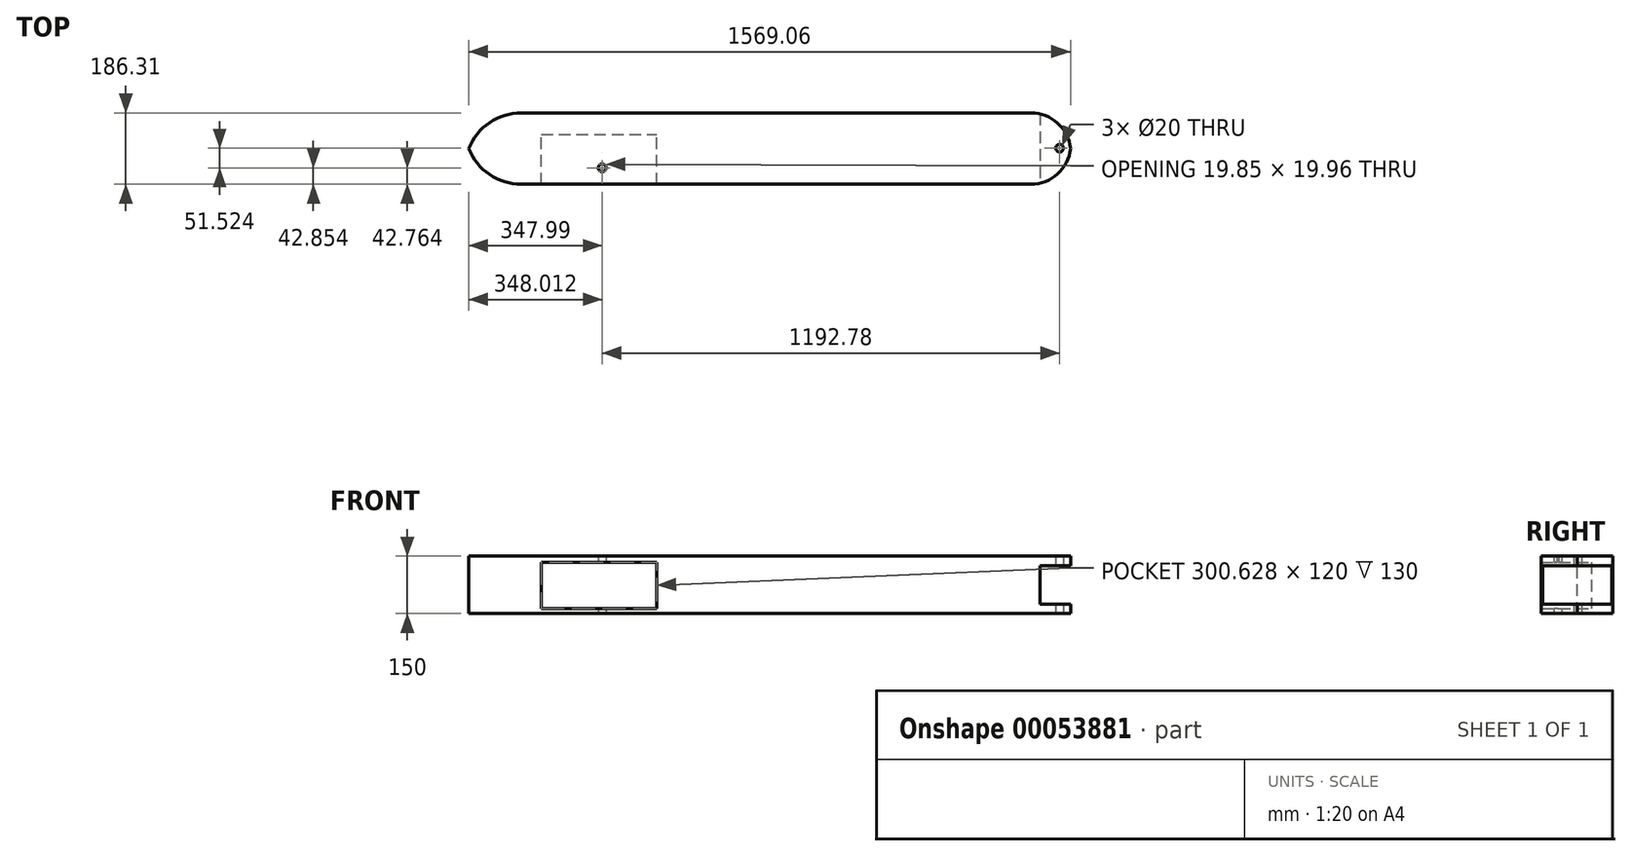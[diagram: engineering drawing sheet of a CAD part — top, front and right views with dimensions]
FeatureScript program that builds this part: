
annotation { "Feature Type Name" : "Feature", "Feature Type Description" : "" }
export const myFeature = defineFeature(function(context is Context, id is Id, definition is map)
    precondition{}
    {
        {
            var Q0;
            Q0=qCreatedBy(makeId("Front.planeOp"),FACE);
            var sketch = newSketch(context, id + "F0", { "sketchPlane" : qUnion([Q0])});
            skLineSegment(sketch, "E0.bottom", {"start": v(-454.56, 147.44) * mm, "end": v(1045.44, 147.44) * mm});
            skLineSegment(sketch, "E0.top", {"start": v(-454.56, -2.56) * mm, "end": v(1045.44, -2.56) * mm});
            skLineSegment(sketch, "E0.left", {"start": v(-454.56, 147.44) * mm, "end": v(-454.56, -2.56) * mm});
            skLineSegment(sketch, "E0.right", {"start": v(1045.44, 147.44) * mm, "end": v(1045.44, -2.56) * mm});
            skSolve(sketch);
        }
        {
            var Q0;
            Q0=makeQuery(id+"F0.imprint","IMPRINT",FACE,{"disambiguationData":[TD([[makeQuery(id+"F0.imprint","IMPRINT",EDGE,{"derivedFrom":sQuery(id+"F0.wireOp",EDGE,"E0.bottom")}),-1.0]])]});
            var Q1;
            Q1=makeQuery(id+"F0.imprint","IMPRINT",FACE,{"disambiguationData":[TD([[makeQuery(id+"F0.imprint","IMPRINT",EDGE,{"derivedFrom":sQuery(id+"F0.wireOp",EDGE,"f0e6ab77-5583-4a0c-8637-5662e6611f36.bottom")}),-1.0]])]});
            extrude(context, id + "F1", {"entities" : qUnion([Q0, Q1]), "depth" : 56.3 * mm});
        }
        {
            var Q0;
            Q0=makeQuery(id+"F1.opExtrude","CAP_FACE",FACE,{"disambiguationData":[OSD([sQuery(id+"F0.wireOp",EDGE,"E0.bottom"),sQuery(id+"F0.wireOp",EDGE,"E0.top"),sQuery(id+"F0.wireOp",EDGE,"E0.left"),sQuery(id+"F0.wireOp",EDGE,"E0.right")])],"isStart":false});
            var sketch = newSketch(context, id + "F2", { "sketchPlane" : qUnion([Q0])});
            skLineSegment(sketch, "E1.bottom", {"start": v(-254.92, 130.96) * mm, "end": v(45.7, 130.96) * mm});
            skLineSegment(sketch, "E1.top", {"start": v(-254.92, 10.96) * mm, "end": v(45.7, 10.96) * mm});
            skLineSegment(sketch, "E1.left", {"start": v(-254.92, 130.96) * mm, "end": v(-254.92, 10.96) * mm});
            skLineSegment(sketch, "E1.right", {"start": v(45.7, 130.96) * mm, "end": v(45.7, 10.96) * mm});
            skSolve(sketch);
        }
        {
            var Q0;
            Q0=makeQuery(id+"F2.imprint","IMPRINT",FACE,{"disambiguationData":[TD([[makeQuery(id+"F2.imprint","IMPRINT",EDGE,{"derivedFrom":sQuery(id+"F2.wireOp",EDGE,"E1.bottom")}),1.0]])]});
            extrude(context, id + "F3", {"entities" : qUnion([Q0]), "operationType" : NewBodyOperationType.ADD, "depth" : 130 * mm});
        }
        {
            var Q0;
            Q0=makeQuery(id+"F3.opExtrude","SWEPT_FACE",FACE,{"disambiguationData":[OSD([sQuery(id+"F2.wireOp",EDGE,"E1.bottom")])]});
            var sketch = newSketch(context, id + "F4", { "sketchPlane" : qUnion([Q0])});
            skCircle(sketch, "E2", {"center": v(-96.12, 143.37) * mm, "radius": 16.52 * mm});
            skCircle(sketch, "E3", {"center": v(-96.12, 143.37) * mm, "radius": 16.28 * mm});
            skSolve(sketch);
        }
        {
            var Q0;
            {var subQ0=sQuery(id+"F0.wireOp",EDGE,"E0.top");Q0=makeQuery(id+"F3.boolean.opBoolean","MERGE",FACE,{"derivedFrom":[makeQuery(id+"F1.opExtrude","SWEPT_FACE",FACE,{"disambiguationData":[OSD([subQ0])]}),makeQuery(id+"F3.opExtrude","SWEPT_FACE",FACE,{"disambiguationData":[OSD([subQ0])]})]});}
            var sketch = newSketch(context, id + "F5", { "sketchPlane" : qUnion([Q0])});
            skCircle(sketch, "E4", {"center": v(-96.16, 143.55) * mm, "radius": 15.74 * mm});
            skSolve(sketch);
        }
        {
            var Q0;
            Q0=sQuery(id+"F4.wireOp",VERTEX,"E3.center");
            var Q1;
            Q1=makeQuery(id+"F1.opExtrude","SWEPT_BODY",BODY,{"disambiguationData":[OSD([sQuery(id+"F0.wireOp",EDGE,"E0.bottom"),sQuery(id+"F0.wireOp",EDGE,"E0.top"),sQuery(id+"F0.wireOp",EDGE,"E0.left"),sQuery(id+"F0.wireOp",EDGE,"E0.right")])]});
            hole(context, id + "F6", {"style" : HoleStyle.SIMPLE, "holeDiameter" : 20 * mm, "endStyle" : HoleEndStyle.THROUGH, "locations" : qUnion([Q0]), "scope" : qUnion([Q1])});
        }
        {
            var Q0;
            Q0=sQuery(id+"F5.wireOp",VERTEX,"E4.center");
            var Q1;
            Q1=makeQuery(id+"F1.opExtrude","SWEPT_BODY",BODY,{"disambiguationData":[OSD([sQuery(id+"F0.wireOp",EDGE,"E0.bottom"),sQuery(id+"F0.wireOp",EDGE,"E0.top"),sQuery(id+"F0.wireOp",EDGE,"E0.left"),sQuery(id+"F0.wireOp",EDGE,"E0.right")])]});
            hole(context, id + "F7", {"style" : HoleStyle.SIMPLE, "holeDiameter" : 20 * mm, "endStyle" : HoleEndStyle.THROUGH, "locations" : qUnion([Q0]), "scope" : qUnion([Q1])});
        }
        {
            var Q0;
            Q0=makeQuery(id+"F3.opExtrude","CAP_EDGE",EDGE,{"disambiguationData":[OSD([sQuery(id+"F0.wireOp",EDGE,"E0.left")])],"isStart":false});
            var Q1;
            Q1=makeQuery(id+"F1.opExtrude","CAP_EDGE",EDGE,{"disambiguationData":[OSD([sQuery(id+"F0.wireOp",EDGE,"E0.left")])],"isStart":true});
            fillet(context, id + "F8", {"entities" : qUnion([Q0, Q1]), "radius" : 147.58 * mm, "tangentPropagation" : true, "allowEdgeOverflow" : false});
        }
        {
            var Q0;
            {var subQ0=sQuery(id+"F0.wireOp",EDGE,"E0.right");Q0=makeQuery(id+"F3.boolean.opBoolean","MERGE",FACE,{"derivedFrom":[makeQuery(id+"F1.opExtrude","SWEPT_FACE",FACE,{"disambiguationData":[OSD([subQ0])]}),makeQuery(id+"F3.opExtrude","SWEPT_FACE",FACE,{"disambiguationData":[OSD([subQ0])]})]});}
            var sketch = newSketch(context, id + "F9", { "sketchPlane" : qUnion([Q0])});
            skLineSegment(sketch, "E5.bottom", {"start": v(0, 122.44) * mm, "end": v(-186.3, 122.44) * mm});
            skLineSegment(sketch, "E5.top", {"start": v(0, 22.44) * mm, "end": v(-186.3, 22.44) * mm});
            skLineSegment(sketch, "E5.left", {"start": v(0, 122.44) * mm, "end": v(0, 22.44) * mm});
            skLineSegment(sketch, "E5.right", {"start": v(-186.3, 122.44) * mm, "end": v(-186.3, 22.44) * mm});
            skSolve(sketch);
        }
        {
            var Q0;
            {var subQ0=sQuery(id+"F9.wireOp",EDGE,"E5.bottom");Q0=makeQuery(id+"F9.imprint","IMPRINT",FACE,{"disambiguationData":[TD([[makeQuery(id+"F9.imprint","IMPRINT",EDGE,{"derivedFrom":subQ0}),-1.0]])]});}
            var Q1;
            {var subQ0=sQuery(id+"F9.wireOp",EDGE,"E5.top");Q1=makeQuery(id+"F9.imprint","IMPRINT",FACE,{"disambiguationData":[TD([[makeQuery(id+"F9.imprint","IMPRINT",EDGE,{"derivedFrom":subQ0}),1.0]])]});}
            extrude(context, id + "F10", {"entities" : qUnion([Q0, Q1]), "operationType" : NewBodyOperationType.ADD, "depth" : 80 * mm});
        }
        {
            var Q0;
            {var subQ0=sQuery(id+"F0.wireOp",EDGE,"E0.right");var subQ2=makeQuery(id+"F1.opExtrude","CAP_EDGE",EDGE,{"disambiguationData":[OSD([subQ0])],"isStart":true});Q0=makeQuery(id+"F10.opExtrude","CAP_EDGE",EDGE,{"disambiguationData":[OSD([subQ0]),TDD([makeQuery(id+"F9.imprint","IMPRINT",EDGE,{"disambiguationData":[TD([[makeQuery(id+"F9.imprint","INTERSECT",VERTEX,{"derivedFrom":[subQ2,sQuery(id+"F9.wireOp",EDGE,"E5.bottom"),sQuery(id+"F9.wireOp",EDGE,"E5.left")]}),1.0]])],"derivedFrom":subQ2})])],"isStart":false});}
            var Q1;
            {var subQ0=sQuery(id+"F0.wireOp",EDGE,"E0.right");var subQ2=makeQuery(id+"F1.opExtrude","CAP_EDGE",EDGE,{"disambiguationData":[OSD([subQ0])],"isStart":true});Q1=makeQuery(id+"F10.opExtrude","CAP_EDGE",EDGE,{"disambiguationData":[OSD([subQ0]),TDD([makeQuery(id+"F9.imprint","IMPRINT",EDGE,{"disambiguationData":[TD([[makeQuery(id+"F9.imprint","INTERSECT",VERTEX,{"derivedFrom":[subQ2,sQuery(id+"F9.wireOp",EDGE,"E5.top"),sQuery(id+"F9.wireOp",EDGE,"E5.left")]}),-1.0]])],"derivedFrom":subQ2})])],"isStart":false});}
            var Q2;
            {var subQ0=sQuery(id+"F0.wireOp",EDGE,"E0.right");var subQ2=makeQuery(id+"F3.opExtrude","CAP_EDGE",EDGE,{"disambiguationData":[OSD([subQ0])],"isStart":false});Q2=makeQuery(id+"F10.opExtrude","CAP_EDGE",EDGE,{"disambiguationData":[OSD([subQ0]),TDD([makeQuery(id+"F9.imprint","IMPRINT",EDGE,{"disambiguationData":[TD([[makeQuery(id+"F9.imprint","INTERSECT",VERTEX,{"derivedFrom":[subQ2,sQuery(id+"F9.wireOp",EDGE,"E5.top"),sQuery(id+"F9.wireOp",EDGE,"E5.right")]}),-1.0]])],"derivedFrom":subQ2})])],"isStart":false});}
            var Q3;
            {var subQ0=sQuery(id+"F0.wireOp",EDGE,"E0.right");var subQ2=makeQuery(id+"F3.opExtrude","CAP_EDGE",EDGE,{"disambiguationData":[OSD([subQ0])],"isStart":false});Q3=makeQuery(id+"F10.opExtrude","CAP_EDGE",EDGE,{"disambiguationData":[OSD([subQ0]),TDD([makeQuery(id+"F9.imprint","IMPRINT",EDGE,{"disambiguationData":[TD([[makeQuery(id+"F9.imprint","INTERSECT",VERTEX,{"derivedFrom":[subQ2,sQuery(id+"F9.wireOp",EDGE,"E5.bottom"),sQuery(id+"F9.wireOp",EDGE,"E5.right")]}),1.0]])],"derivedFrom":subQ2})])],"isStart":false});}
            fillet(context, id + "F11", {"entities" : qUnion([Q0, Q1, Q2, Q3]), "radius" : 103.66 * mm, "tangentPropagation" : true, "allowEdgeOverflow" : false});
        }
        {
            var Q0;
            {var subQ0=sQuery(id+"F0.wireOp",EDGE,"E0.top");Q0=makeQuery(id+"F10.boolean.opBoolean","MERGE",FACE,{"derivedFrom":[makeQuery(id+"F3.boolean.opBoolean","MERGE",FACE,{"derivedFrom":[makeQuery(id+"F1.opExtrude","SWEPT_FACE",FACE,{"disambiguationData":[OSD([subQ0])]}),makeQuery(id+"F3.opExtrude","SWEPT_FACE",FACE,{"disambiguationData":[OSD([subQ0])]})]}),makeQuery(id+"F10.opExtrude","SWEPT_FACE",FACE,{"disambiguationData":[OSD([subQ0,sQuery(id+"F0.wireOp",EDGE,"E0.right")])]})]});}
            var sketch = newSketch(context, id + "F12", { "sketchPlane" : qUnion([Q0])});
            skCircle(sketch, "E6", {"center": v(1096.62, 92.02) * mm, "radius": 12.94 * mm});
            skCircle(sketch, "E7", {"center": v(1096.62, 92.02) * mm, "radius": 12.91 * mm});
            skSolve(sketch);
        }
        {
            var Q0;
            Q0=sQuery(id+"F12.wireOp",VERTEX,"E6.center");
            var Q1;
            Q1=makeQuery(id+"F1.opExtrude","SWEPT_BODY",BODY,{"disambiguationData":[OSD([sQuery(id+"F0.wireOp",EDGE,"E0.bottom"),sQuery(id+"F0.wireOp",EDGE,"E0.top"),sQuery(id+"F0.wireOp",EDGE,"E0.left"),sQuery(id+"F0.wireOp",EDGE,"E0.right")])]});
            hole(context, id + "F13", {"style" : HoleStyle.SIMPLE, "holeDiameter" : 20 * mm, "endStyle" : HoleEndStyle.THROUGH, "locations" : qUnion([Q0]), "scope" : qUnion([Q1])});
        }
    });
